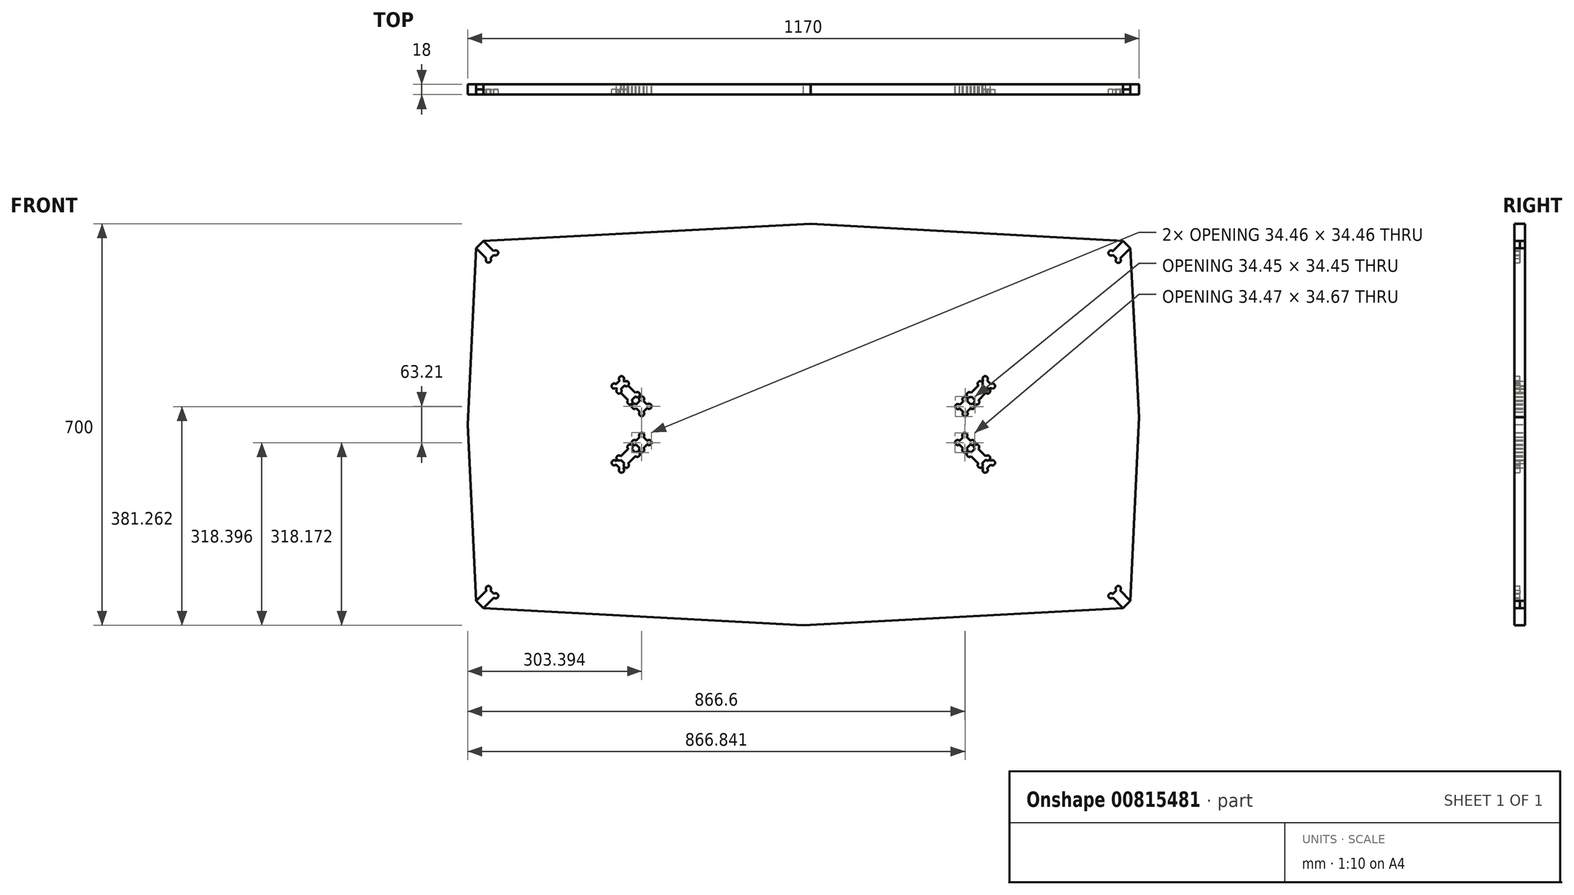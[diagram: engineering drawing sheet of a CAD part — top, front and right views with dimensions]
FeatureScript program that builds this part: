
annotation { "Feature Type Name" : "Feature", "Feature Type Description" : "" }
export const myFeature = defineFeature(function(context is Context, id is Id, definition is map)
    precondition{}
    {
        {
            var Q0;
            Q0=qCreatedBy(makeId("Front.planeOp"),FACE);
            var sketch = newSketch(context, id + "F0", { "sketchPlane" : qUnion([Q0])});
            skLineSegment(sketch, "E0.bottom", {"start": v(-557.27, 320) * mm, "end": v(557.27, 320) * mm});
            skLineSegment(sketch, "E0.top", {"start": v(-557.27, -320) * mm, "end": v(557.27, -320) * mm});
            skLineSegment(sketch, "E0.left", {"start": v(-570, 307.27) * mm, "end": v(-570, -307.27) * mm});
            skLineSegment(sketch, "E0.right", {"start": v(570, 307.27) * mm, "end": v(570, -307.27) * mm});
            skPoint(sketch, "E0.middle", {"position": v(0, 0) * mm});
            skLineSegment(sketch, "E1", {"start": v(557.27, 320) * mm, "end": v(570, 307.27) * mm});
            skPoint(sketch, "E2.orphan", {"position": v(570, 320) * mm});
            skLineSegment(sketch, "E3", {"start": v(570, 307.27) * mm, "end": v(551.97, 289.24) * mm});
            skLineSegment(sketch, "E4", {"start": v(557.27, 320) * mm, "end": v(539.24, 301.97) * mm});
            skLineSegment(sketch, "E5", {"start": v(570, -307.27) * mm, "end": v(557.27, -320) * mm});
            skPoint(sketch, "E6.orphan", {"position": v(570, -320) * mm});
            skLineSegment(sketch, "E7", {"start": v(570, -307.27) * mm, "end": v(551.97, -289.24) * mm});
            skLineSegment(sketch, "E8", {"start": v(557.27, -320) * mm, "end": v(539.24, -301.97) * mm});
            skLineSegment(sketch, "E9", {"start": v(-570, -307.27) * mm, "end": v(-557.27, -320) * mm});
            skPoint(sketch, "E10.orphan", {"position": v(-570, -320) * mm});
            skLineSegment(sketch, "E11", {"start": v(-570, -307.27) * mm, "end": v(-551.97, -289.24) * mm});
            skLineSegment(sketch, "E12", {"start": v(-557.27, -320) * mm, "end": v(-539.24, -301.97) * mm});
            skLineSegment(sketch, "E13", {"start": v(-557.27, 320) * mm, "end": v(-570, 307.27) * mm});
            skPoint(sketch, "E14.orphan", {"position": v(-570, 320) * mm});
            skLineSegment(sketch, "E15", {"start": v(-557.27, 320) * mm, "end": v(-539.45, 302.18) * mm});
            skLineSegment(sketch, "E16", {"start": v(-570, 307.27) * mm, "end": v(-552.19, 289.46) * mm});
            skLineSegment(sketch, "E17", {"start": v(-545.35, 289.5) * mm, "end": v(-539.07, 295.78) * mm});
            skLineSegment(sketch, "E18", {"start": v(545.6, -289.24) * mm, "end": v(539.24, -295.6) * mm});
            skLineSegment(sketch, "E19", {"start": v(539.24, 295.6) * mm, "end": v(545.6, 289.24) * mm});
            skLineSegment(sketch, "E20", {"start": v(-545.6, -289.24) * mm, "end": v(-539.24, -295.6) * mm});
            skLineSegment(sketch, "E21", {"start": v(-326.4, 70.04) * mm, "end": v(-320.04, 76.4) * mm});
            skLineSegment(sketch, "E22", {"start": v(-326.4, 63.67) * mm, "end": v(-324.28, 61.55) * mm});
            skLineSegment(sketch, "E23", {"start": v(-313.67, 76.4) * mm, "end": v(-311.55, 74.28) * mm});
            skLineSegment(sketch, "E24", {"start": v(-311.55, 67.92) * mm, "end": v(-317.92, 61.55) * mm});
            skLineSegment(sketch, "E25", {"start": v(-317.92, 55.19) * mm, "end": v(-305.19, 42.46) * mm});
            skLineSegment(sketch, "E26", {"start": v(-305.19, 67.92) * mm, "end": v(-292.54, 55.27) * mm});
            skLineSegment(sketch, "E27", {"start": v(-298.82, 42.46) * mm, "end": v(-292.55, 48.73) * mm});
            skLineSegment(sketch, "E28", {"start": v(-284.79, 41.15) * mm, "end": v(-291.15, 34.79) * mm});
            skLineSegment(sketch, "E29", {"start": v(-278.42, 41.15) * mm, "end": v(-272.06, 34.79) * mm});
            skLineSegment(sketch, "E30", {"start": v(-291.15, 28.42) * mm, "end": v(-284.79, 22.06) * mm});
            skLineSegment(sketch, "E31", {"start": v(-272.06, 28.42) * mm, "end": v(-278.42, 22.06) * mm});
            skLineSegment(sketch, "E32", {"start": v(-548.79, 286.06) * mm, "end": v(-545.85, 283.12) * mm});
            skLineSegment(sketch, "E33", {"start": v(-326.4, -63.67) * mm, "end": v(-324.28, -61.55) * mm});
            skLineSegment(sketch, "E34", {"start": v(-326.4, -70.04) * mm, "end": v(-320.04, -76.4) * mm});
            skLineSegment(sketch, "E35", {"start": v(-317.92, -61.55) * mm, "end": v(-311.55, -67.91) * mm});
            skLineSegment(sketch, "E36", {"start": v(-313.67, -76.4) * mm, "end": v(-308.37, -71.1) * mm});
            skLineSegment(sketch, "E37", {"start": v(-317.92, -55.19) * mm, "end": v(-305.19, -42.46) * mm});
            skLineSegment(sketch, "E38", {"start": v(-305.19, -67.91) * mm, "end": v(-292.46, -55.19) * mm});
            skLineSegment(sketch, "E39", {"start": v(-298.82, -42.46) * mm, "end": v(-292.46, -48.82) * mm});
            skLineSegment(sketch, "E40", {"start": v(-291.15, -34.79) * mm, "end": v(-284.79, -41.15) * mm});
            skLineSegment(sketch, "E41", {"start": v(-291.15, -28.42) * mm, "end": v(-284.79, -22.06) * mm});
            skLineSegment(sketch, "E42", {"start": v(-278.42, -41.15) * mm, "end": v(-272.06, -34.79) * mm});
            skLineSegment(sketch, "E43", {"start": v(-278.42, -22.06) * mm, "end": v(-272.06, -28.42) * mm});
            skLineSegment(sketch, "E44", {"start": v(-557.27, 320) * mm, "end": v(12.73, 350) * mm});
            skLineSegment(sketch, "E45", {"start": v(12.73, 350) * mm, "end": v(557.27, 320) * mm});
            skLineSegment(sketch, "E46", {"start": v(-557.27, -320) * mm, "end": v(0, -350) * mm});
            skLineSegment(sketch, "E47", {"start": v(0, -350) * mm, "end": v(557.27, -320) * mm});
            skLineSegment(sketch, "E48", {"start": v(-570, -307.27) * mm, "end": v(-585, 0) * mm});
            skLineSegment(sketch, "E49", {"start": v(-585, 0) * mm, "end": v(-570, 307.27) * mm});
            skLineSegment(sketch, "E50", {"start": v(570, -307.27) * mm, "end": v(585, 12.73) * mm});
            skLineSegment(sketch, "E51", {"start": v(585, 12.73) * mm, "end": v(570, 307.27) * mm});
            skLineSegment(sketch, "E52", {"start": v(320.04, -76.4) * mm, "end": v(326.4, -70.04) * mm});
            skLineSegment(sketch, "E53", {"start": v(313.67, -76.4) * mm, "end": v(311.55, -74.28) * mm});
            skLineSegment(sketch, "E54", {"start": v(311.55, -67.92) * mm, "end": v(317.91, -61.55) * mm});
            skLineSegment(sketch, "E55", {"start": v(324.28, -61.55) * mm, "end": v(326.4, -63.67) * mm});
            skLineSegment(sketch, "E56", {"start": v(305.19, -67.92) * mm, "end": v(292.46, -55.19) * mm});
            skLineSegment(sketch, "E57", {"start": v(317.91, -55.19) * mm, "end": v(305.19, -42.46) * mm});
            skLineSegment(sketch, "E58", {"start": v(298.82, -42.46) * mm, "end": v(292.46, -48.82) * mm});
            skLineSegment(sketch, "E59", {"start": v(291.15, -34.79) * mm, "end": v(284.55, -41.39) * mm});
            skLineSegment(sketch, "E60", {"start": v(278.53, -41.26) * mm, "end": v(272.06, -34.79) * mm});
            skLineSegment(sketch, "E61", {"start": v(291.15, -28.42) * mm, "end": v(284.66, -21.94) * mm});
            skLineSegment(sketch, "E62", {"start": v(278.2, -22.28) * mm, "end": v(272.03, -28.45) * mm});
            skLineSegment(sketch, "E63", {"start": v(326.4, 63.67) * mm, "end": v(324.28, 61.55) * mm});
            skLineSegment(sketch, "E64", {"start": v(326.4, 70.04) * mm, "end": v(320.04, 76.4) * mm});
            skLineSegment(sketch, "E65", {"start": v(313.67, 76.4) * mm, "end": v(311.44, 74.17) * mm});
            skLineSegment(sketch, "E66", {"start": v(311.47, 67.83) * mm, "end": v(317.89, 61.52) * mm});
            skLineSegment(sketch, "E67", {"start": v(317.94, 55.16) * mm, "end": v(305.33, 42.32) * mm});
            skLineSegment(sketch, "E68", {"start": v(305.1, 67.78) * mm, "end": v(292.49, 54.94) * mm});
            skLineSegment(sketch, "E69", {"start": v(292.54, 48.57) * mm, "end": v(298.96, 42.27) * mm});
            skLineSegment(sketch, "E70", {"start": v(291.36, 34.53) * mm, "end": v(284.94, 40.84) * mm});
            skLineSegment(sketch, "E71", {"start": v(278.58, 40.78) * mm, "end": v(272.27, 34.36) * mm});
            skLineSegment(sketch, "E72", {"start": v(291.41, 28.16) * mm, "end": v(285.1, 21.74) * mm});
            skLineSegment(sketch, "E73", {"start": v(272.32, 28) * mm, "end": v(278.74, 21.69) * mm});
            skArc(sketch, "E74", {"start": v(-313.67, 76.4) * mm, "mid": v(-316.85, 84.08) * mm, "end": v(-320.04, 76.4) * mm});
            skArc(sketch, "E75", {"start": v(-326.4, 70.04) * mm, "mid": v(-334.08, 66.85) * mm, "end": v(-326.4, 63.67) * mm});
            skArc(sketch, "E76", {"start": v(-326.4, -63.67) * mm, "mid": v(-334.08, -66.85) * mm, "end": v(-326.4, -70.04) * mm});
            skArc(sketch, "E77", {"start": v(-320.04, -76.4) * mm, "mid": v(-316.86, -84.08) * mm, "end": v(-313.67, -76.4) * mm});
            skArc(sketch, "E78", {"start": v(313.67, -76.4) * mm, "mid": v(316.85, -84.08) * mm, "end": v(320.04, -76.4) * mm});
            skArc(sketch, "E79", {"start": v(326.4, -70.04) * mm, "mid": v(334.08, -66.86) * mm, "end": v(326.4, -63.67) * mm});
            skArc(sketch, "E80", {"start": v(320.04, 76.4) * mm, "mid": v(316.86, 84.08) * mm, "end": v(313.67, 76.4) * mm});
            skArc(sketch, "E81", {"start": v(326.4, 63.67) * mm, "mid": v(334.08, 66.85) * mm, "end": v(326.4, 70.04) * mm});
            skArc(sketch, "E82", {"start": v(311.47, 67.83) * mm, "mid": v(308.22, 75.49) * mm, "end": v(305.1, 67.78) * mm});
            skArc(sketch, "E83", {"start": v(317.94, 55.16) * mm, "mid": v(325.6, 58.4) * mm, "end": v(317.89, 61.52) * mm});
            skArc(sketch, "E84", {"start": v(317.91, -61.55) * mm, "mid": v(325.6, -58.37) * mm, "end": v(317.91, -55.19) * mm});
            skArc(sketch, "E85", {"start": v(305.19, -67.92) * mm, "mid": v(308.37, -75.6) * mm, "end": v(311.55, -67.92) * mm});
            skArc(sketch, "E86", {"start": v(-317.92, -55.19) * mm, "mid": v(-325.6, -58.37) * mm, "end": v(-317.92, -61.55) * mm});
            skArc(sketch, "E87", {"start": v(-311.55, -67.91) * mm, "mid": v(-308.37, -75.6) * mm, "end": v(-305.19, -67.91) * mm});
            skArc(sketch, "E88", {"start": v(-298.82, -42.46) * mm, "mid": v(-302, -34.78) * mm, "end": v(-305.19, -42.46) * mm});
            skArc(sketch, "E89", {"start": v(-292.46, -55.19) * mm, "mid": v(-284.78, -52) * mm, "end": v(-292.46, -48.82) * mm});
            skArc(sketch, "E90", {"start": v(-278.42, -22.06) * mm, "mid": v(-281.6, -14.38) * mm, "end": v(-284.79, -22.06) * mm});
            skArc(sketch, "E91", {"start": v(-272.06, -34.79) * mm, "mid": v(-264.38, -31.6) * mm, "end": v(-272.06, -28.42) * mm});
            skArc(sketch, "E92", {"start": v(-291.15, -28.42) * mm, "mid": v(-298.83, -31.6) * mm, "end": v(-291.15, -34.79) * mm});
            skArc(sketch, "E93", {"start": v(-284.79, -41.15) * mm, "mid": v(-281.6, -48.83) * mm, "end": v(-278.42, -41.15) * mm});
            skArc(sketch, "E94", {"start": v(-311.55, 67.92) * mm, "mid": v(-303.87, 71.1) * mm, "end": v(-311.55, 74.28) * mm});
            skArc(sketch, "E95", {"start": v(-324.28, 61.55) * mm, "mid": v(-321.1, 53.87) * mm, "end": v(-317.92, 61.55) * mm});
            skArc(sketch, "E96", {"start": v(-292.55, 48.73) * mm, "mid": v(-284.95, 51.98) * mm, "end": v(-292.54, 55.27) * mm});
            skArc(sketch, "E97", {"start": v(-305.19, 42.46) * mm, "mid": v(-302, 34.78) * mm, "end": v(-298.82, 42.46) * mm});
            skArc(sketch, "E98", {"start": v(-291.15, 34.79) * mm, "mid": v(-298.83, 31.6) * mm, "end": v(-291.15, 28.42) * mm});
            skArc(sketch, "E99", {"start": v(-278.42, 41.15) * mm, "mid": v(-281.6, 48.83) * mm, "end": v(-284.79, 41.15) * mm});
            skArc(sketch, "E100", {"start": v(-272.06, 28.42) * mm, "mid": v(-264.38, 31.6) * mm, "end": v(-272.06, 34.79) * mm});
            skArc(sketch, "E101", {"start": v(-284.79, 22.06) * mm, "mid": v(-281.6, 14.38) * mm, "end": v(-278.42, 22.06) * mm});
            skArc(sketch, "E102", {"start": v(305.19, -42.46) * mm, "mid": v(302, -34.78) * mm, "end": v(298.82, -42.46) * mm});
            skArc(sketch, "E103", {"start": v(292.46, -48.82) * mm, "mid": v(284.78, -52) * mm, "end": v(292.46, -55.19) * mm});
            skArc(sketch, "E104", {"start": v(278.53, -41.26) * mm, "mid": v(281.36, -49.16) * mm, "end": v(284.55, -41.39) * mm});
            skArc(sketch, "E105", {"start": v(291.15, -34.79) * mm, "mid": v(298.83, -31.6) * mm, "end": v(291.15, -28.42) * mm});
            skArc(sketch, "E106", {"start": v(284.66, -21.94) * mm, "mid": v(281.03, -14.5) * mm, "end": v(278.2, -22.28) * mm});
            skArc(sketch, "E107", {"start": v(272.05, -28.43) * mm, "mid": v(264.37, -31.62) * mm, "end": v(272.06, -34.79) * mm});
            skPoint(sketch, "E108.orphan", {"position": v(268.54, -31.94) * mm});
            skPoint(sketch, "E109.end.orphan", {"position": v(268.54, -31.3) * mm});
            skArc(sketch, "E110", {"start": v(292.49, 54.94) * mm, "mid": v(284.83, 51.69) * mm, "end": v(292.54, 48.57) * mm});
            skArc(sketch, "E111", {"start": v(298.96, 42.27) * mm, "mid": v(302.21, 34.61) * mm, "end": v(305.33, 42.32) * mm});
            skArc(sketch, "E112", {"start": v(284.94, 40.84) * mm, "mid": v(281.7, 48.49) * mm, "end": v(278.58, 40.78) * mm});
            skArc(sketch, "E113", {"start": v(291.41, 28.16) * mm, "mid": v(299.07, 31.41) * mm, "end": v(291.36, 34.53) * mm});
            skArc(sketch, "E114", {"start": v(272.27, 34.36) * mm, "mid": v(264.61, 31.11) * mm, "end": v(272.32, 28) * mm});
            skArc(sketch, "E115", {"start": v(278.74, 21.69) * mm, "mid": v(282, 14.04) * mm, "end": v(285.1, 21.74) * mm});
            skArc(sketch, "E116", {"start": v(-545.6, -289.24) * mm, "mid": v(-548.79, -281.56) * mm, "end": v(-551.97, -289.24) * mm});
            skArc(sketch, "E117", {"start": v(-539.24, -301.97) * mm, "mid": v(-531.56, -298.79) * mm, "end": v(-539.24, -295.6) * mm});
            skArc(sketch, "E118", {"start": v(-552.19, 289.46) * mm, "mid": v(-548.73, 282.05) * mm, "end": v(-545.35, 289.5) * mm});
            skArc(sketch, "E119", {"start": v(-539.07, 295.78) * mm, "mid": v(-531.61, 299.43) * mm, "end": v(-539.45, 302.18) * mm});
            skArc(sketch, "E120", {"start": v(539.24, 301.97) * mm, "mid": v(531.56, 298.79) * mm, "end": v(539.24, 295.6) * mm});
            skArc(sketch, "E121", {"start": v(545.6, 289.24) * mm, "mid": v(548.79, 281.56) * mm, "end": v(551.97, 289.24) * mm});
            skArc(sketch, "E122", {"start": v(539.24, -295.6) * mm, "mid": v(531.56, -298.79) * mm, "end": v(539.24, -301.97) * mm});
            skArc(sketch, "E123", {"start": v(551.97, -289.24) * mm, "mid": v(548.79, -281.56) * mm, "end": v(545.6, -289.24) * mm});
            skLineSegment(sketch, "E124.trimOffspring", {"start": v(-332.77, 70.04) * mm, "end": v(-329.58, 66.85) * mm});
            skSolve(sketch);
        }
        {
            var Q0;
            {var subQ0=sQuery(id+"F0.wireOp",EDGE,"E13");Q0=makeQuery(id+"F0.imprint","IMPRINT",FACE,{"disambiguationData":[TD([[makeQuery(id+"F0.imprint","IMPRINT",EDGE,{"derivedFrom":subQ0}),1.0]])]});}
            var sketch = newSketch(context, id + "F1", { "sketchPlane" : qUnion([Q0])});
            skSolve(sketch);
        }
        {
            var Q0;
            Q0=makeQuery(id+"F0.imprint","IMPRINT",FACE,{"disambiguationData":[TD([[makeQuery(id+"F0.imprint","IMPRINT",EDGE,{"derivedFrom":sQuery(id+"F0.wireOp",EDGE,"E9")}),1.0]])]});
            var sketch = newSketch(context, id + "F2", { "sketchPlane" : qUnion([Q0])});
            skSolve(sketch);
        }
        {
            var Q0;
            Q0=makeQuery(id+"F0.imprint","IMPRINT",FACE,{"disambiguationData":[TD([[makeQuery(id+"F0.imprint","IMPRINT",EDGE,{"derivedFrom":sQuery(id+"F0.wireOp",EDGE,"E1")}),-1.0]])]});
            var sketch = newSketch(context, id + "F3", { "sketchPlane" : qUnion([Q0])});
            skSolve(sketch);
        }
        {
            var Q0;
            Q0=makeQuery(id+"F0.imprint","IMPRINT",FACE,{"disambiguationData":[TD([[makeQuery(id+"F0.imprint","IMPRINT",EDGE,{"derivedFrom":sQuery(id+"F0.wireOp",EDGE,"E5")}),-1.0]])]});
            var sketch = newSketch(context, id + "F4", { "sketchPlane" : qUnion([Q0])});
            skSolve(sketch);
        }
        {
            var Q0;
            {var subQ0=sQuery(id+"F0.wireOp",EDGE,"E0.bottom");Q0=makeQuery(id+"F0.imprint","IMPRINT",FACE,{"disambiguationData":[TD([[makeQuery(id+"F0.imprint","IMPRINT",EDGE,{"derivedFrom":subQ0}),-1.0]])]});}
            extrude(context, id + "F5", {"entities" : qUnion([Q0]), "depth" : 18 * mm, "offsetDistance" : 25 * mm});
        }
        {
            var Q0;
            {var subQ0=sQuery(id+"F0.wireOp",EDGE,"E13");Q0=makeQuery(id+"F1.imprint","IMPRINT",FACE,{"disambiguationData":[TD([[makeQuery(id+"F1.imprint","IMPRINT",EDGE,{"derivedFrom":makeQuery(id+"F0.imprint","IMPRINT",EDGE,{"derivedFrom":subQ0})}),1.0]])]});}
            extrude(context, id + "F6", {"entities" : qUnion([Q0]), "operationType" : NewBodyOperationType.ADD, "depth" : 9 * mm, "offsetDistance" : 25 * mm});
        }
        {
            var Q0;
            Q0=makeQuery(id+"F2.imprint","IMPRINT",FACE,{"disambiguationData":[TD([[makeQuery(id+"F2.imprint","IMPRINT",EDGE,{"derivedFrom":makeQuery(id+"F0.imprint","IMPRINT",EDGE,{"derivedFrom":sQuery(id+"F0.wireOp",EDGE,"E9")})}),1.0]])]});
            extrude(context, id + "F7", {"entities" : qUnion([Q0]), "operationType" : NewBodyOperationType.ADD, "depth" : 9 * mm, "offsetDistance" : 25 * mm});
        }
        {
            var Q0;
            Q0=makeQuery(id+"F4.imprint","IMPRINT",FACE,{"disambiguationData":[TD([[makeQuery(id+"F4.imprint","IMPRINT",EDGE,{"derivedFrom":makeQuery(id+"F0.imprint","IMPRINT",EDGE,{"derivedFrom":sQuery(id+"F0.wireOp",EDGE,"E5")})}),-1.0]])]});
            extrude(context, id + "F8", {"entities" : qUnion([Q0]), "operationType" : NewBodyOperationType.ADD, "depth" : 9 * mm, "offsetDistance" : 25 * mm});
        }
        {
            var Q0;
            Q0=makeQuery(id+"F3.imprint","IMPRINT",FACE,{"disambiguationData":[TD([[makeQuery(id+"F3.imprint","IMPRINT",EDGE,{"derivedFrom":makeQuery(id+"F0.imprint","IMPRINT",EDGE,{"derivedFrom":sQuery(id+"F0.wireOp",EDGE,"E1")})}),-1.0]])]});
            extrude(context, id + "F9", {"entities" : qUnion([Q0]), "operationType" : NewBodyOperationType.ADD, "depth" : 9 * mm, "offsetDistance" : 25 * mm});
        }
        {
            var Q0;
            Q0=makeQuery(id+"F0.imprint","IMPRINT",FACE,{"disambiguationData":[TD([[makeQuery(id+"F0.imprint","IMPRINT",EDGE,{"derivedFrom":sQuery(id+"F0.wireOp",EDGE,"E21")}),-1.0]])]});
            var sketch = newSketch(context, id + "F10", { "sketchPlane" : qUnion([Q0])});
            skSolve(sketch);
        }
        {
            var Q0;
            Q0=makeQuery(id+"F10.imprint","IMPRINT",FACE,{"disambiguationData":[TD([[makeQuery(id+"F10.imprint","IMPRINT",EDGE,{"derivedFrom":makeQuery(id+"F0.imprint","IMPRINT",EDGE,{"derivedFrom":sQuery(id+"F0.wireOp",EDGE,"E21")})}),-1.0]])]});
            extrude(context, id + "F11", {"entities" : qUnion([Q0]), "operationType" : NewBodyOperationType.ADD, "depth" : 9 * mm, "offsetDistance" : 25 * mm});
        }
        {
            var Q0;
            Q0=makeQuery(id+"F0.imprint","IMPRINT",FACE,{"disambiguationData":[TD([[makeQuery(id+"F0.imprint","IMPRINT",EDGE,{"derivedFrom":sQuery(id+"F0.wireOp",EDGE,"E33")}),-1.0]])]});
            var sketch = newSketch(context, id + "F12", { "sketchPlane" : qUnion([Q0])});
            skSolve(sketch);
        }
        {
            var Q0;
            Q0=makeQuery(id+"F12.imprint","IMPRINT",FACE,{"disambiguationData":[TD([[makeQuery(id+"F12.imprint","IMPRINT",EDGE,{"derivedFrom":makeQuery(id+"F0.imprint","IMPRINT",EDGE,{"derivedFrom":sQuery(id+"F0.wireOp",EDGE,"E33")})}),-1.0]])]});
            extrude(context, id + "F13", {"entities" : qUnion([Q0]), "operationType" : NewBodyOperationType.ADD, "depth" : 9 * mm, "offsetDistance" : 25 * mm});
        }
        {
            var Q0;
            Q0=makeQuery(id+"F0.imprint","IMPRINT",FACE,{"disambiguationData":[TD([[makeQuery(id+"F0.imprint","IMPRINT",EDGE,{"derivedFrom":sQuery(id+"F0.wireOp",EDGE,"E0.bottom")}),1.0]])]});
            var sketch = newSketch(context, id + "F14", { "sketchPlane" : qUnion([Q0])});
            skSolve(sketch);
        }
        {
            var Q0;
            Q0=makeQuery(id+"F14.imprint","IMPRINT",FACE,{"disambiguationData":[TD([[makeQuery(id+"F14.imprint","IMPRINT",EDGE,{"derivedFrom":makeQuery(id+"F0.imprint","IMPRINT",EDGE,{"derivedFrom":sQuery(id+"F0.wireOp",EDGE,"E0.bottom")})}),1.0]])]});
            extrude(context, id + "F15", {"entities" : qUnion([Q0]), "operationType" : NewBodyOperationType.ADD, "depth" : 18 * mm, "offsetDistance" : 25 * mm});
        }
        {
            var Q0;
            Q0=makeQuery(id+"F0.imprint","IMPRINT",FACE,{"disambiguationData":[TD([[makeQuery(id+"F0.imprint","IMPRINT",EDGE,{"derivedFrom":sQuery(id+"F0.wireOp",EDGE,"E0.left")}),-1.0]])]});
            extrude(context, id + "F16", {"entities" : qUnion([Q0]), "operationType" : NewBodyOperationType.ADD, "depth" : 18 * mm, "offsetDistance" : 25 * mm});
        }
        {
            var Q0;
            Q0=makeQuery(id+"F0.imprint","IMPRINT",FACE,{"disambiguationData":[TD([[makeQuery(id+"F0.imprint","IMPRINT",EDGE,{"derivedFrom":sQuery(id+"F0.wireOp",EDGE,"E0.top")}),-1.0]])]});
            extrude(context, id + "F17", {"entities" : qUnion([Q0]), "operationType" : NewBodyOperationType.ADD, "depth" : 18 * mm, "offsetDistance" : 25 * mm});
        }
        {
            var Q0;
            Q0=makeQuery(id+"F0.imprint","IMPRINT",FACE,{"disambiguationData":[TD([[makeQuery(id+"F0.imprint","IMPRINT",EDGE,{"derivedFrom":sQuery(id+"F0.wireOp",EDGE,"E0.right")}),1.0]])]});
            extrude(context, id + "F18", {"entities" : qUnion([Q0]), "operationType" : NewBodyOperationType.ADD, "depth" : 18 * mm, "offsetDistance" : 25 * mm});
        }
        {
            var Q0;
            Q0=makeQuery(id+"F0.imprint","IMPRINT",FACE,{"disambiguationData":[TD([[makeQuery(id+"F0.imprint","IMPRINT",EDGE,{"derivedFrom":sQuery(id+"F0.wireOp",EDGE,"E52")}),1.0]])]});
            extrude(context, id + "F19", {"entities" : qUnion([Q0]), "operationType" : NewBodyOperationType.ADD, "depth" : 9 * mm, "offsetDistance" : 25 * mm});
        }
        {
            var Q0;
            Q0=makeQuery(id+"F0.imprint","IMPRINT",FACE,{"disambiguationData":[TD([[makeQuery(id+"F0.imprint","IMPRINT",EDGE,{"derivedFrom":sQuery(id+"F0.wireOp",EDGE,"E63")}),-1.0]])]});
            extrude(context, id + "F20", {"entities" : qUnion([Q0]), "operationType" : NewBodyOperationType.ADD, "depth" : 9 * mm, "offsetDistance" : 25 * mm});
        }
    });
